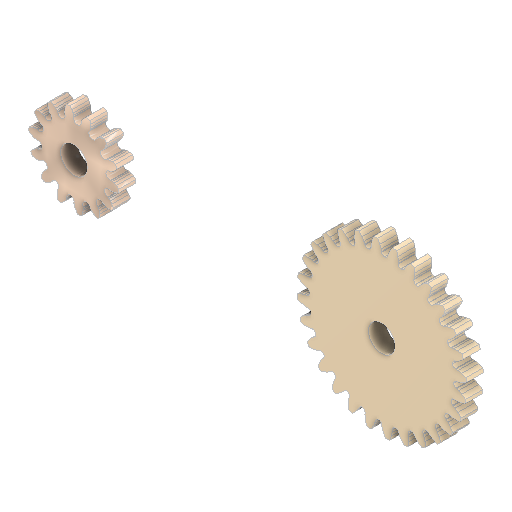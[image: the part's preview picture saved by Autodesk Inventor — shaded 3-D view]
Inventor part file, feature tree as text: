
AUTODESK INVENTOR PART (.ipt)
format: ipt  version: 2025.3 (Build 293356030, 356C)  size: 1,334,784 bytes
history: native  units: mm
features: other x2, extrude x2, sketch x1
ambient origin geometry x8: Origin, YZ Plane, XZ Plane, XY Plane, X Axis, Y Axis, Z Axis, Center Point
bodies: Body1 (feature_tree), Body2 (feature_tree)
feature tree (5):
  other  "small gear"
  sketch  "草圖2"
  extrude  "擠出6"  Depth=3.0mm TaperAngle=0.0deg
  extrude  "擠出7"  Depth=3.0mm TaperAngle=0.0deg
  other  "big gear"
